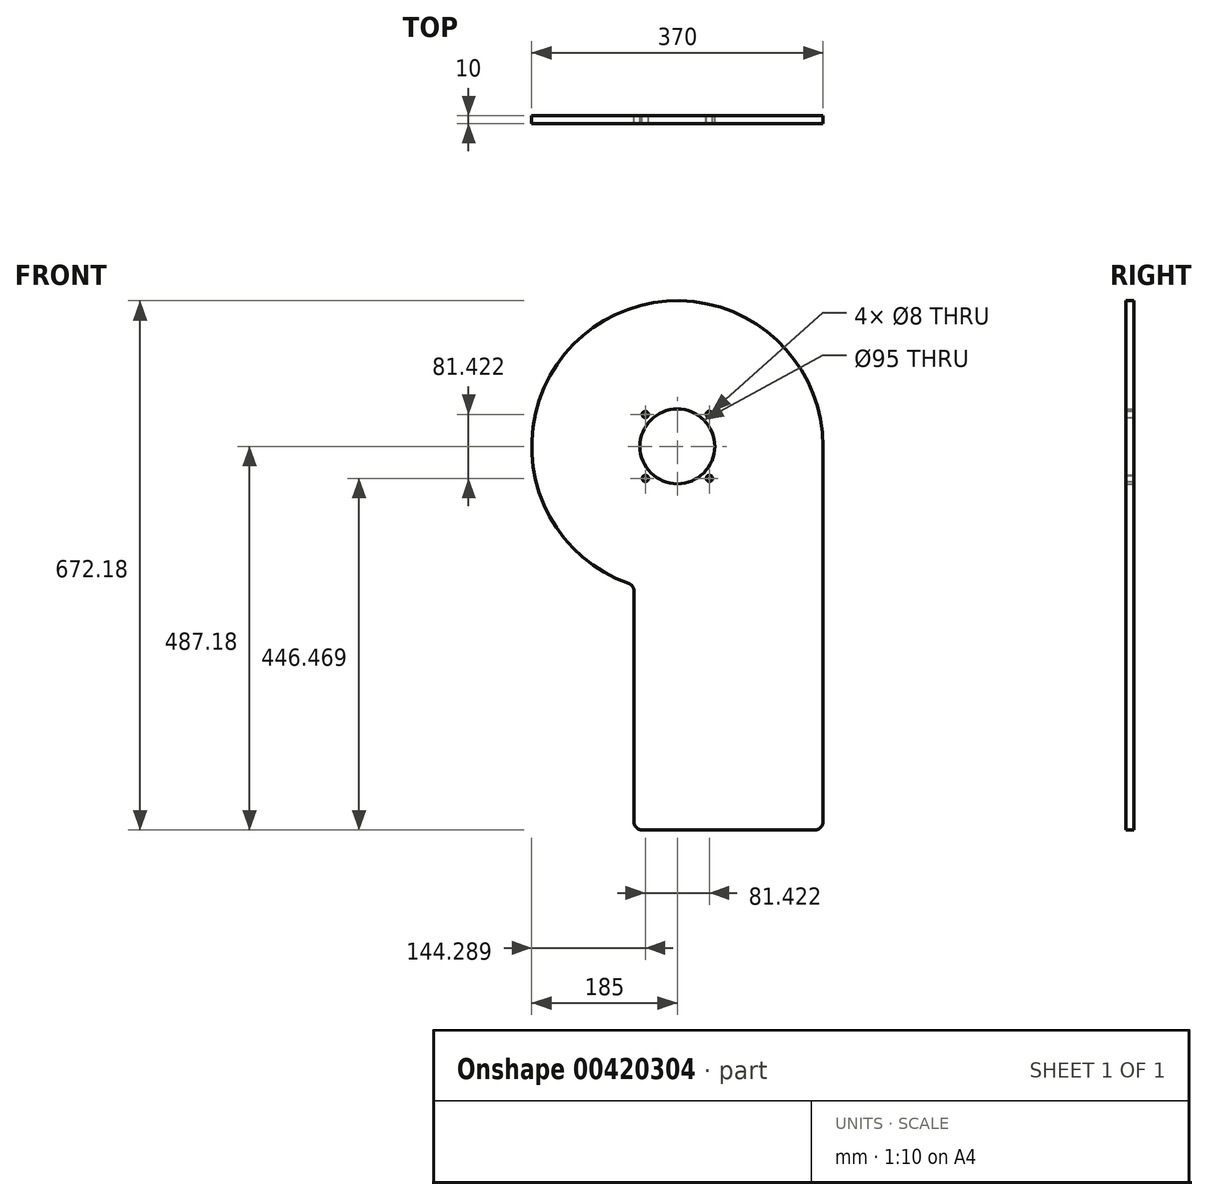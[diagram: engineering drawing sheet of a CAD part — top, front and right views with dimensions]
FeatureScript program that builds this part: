
annotation { "Feature Type Name" : "Feature", "Feature Type Description" : "" }
export const myFeature = defineFeature(function(context is Context, id is Id, definition is map)
    precondition{}
    {
        {
            var Q0;
            Q0=qCreatedBy(makeId("Front.planeOp"),FACE);
            var sketch = newSketch(context, id + "F0", { "sketchPlane" : qUnion([Q0])});
            skCircle(sketch, "E0", {"center": v(185, 1015) * mm, "radius": 47.5 * mm});
            skCircle(sketch, "E1", {"center": v(144.29, 1055.6) * mm, "radius": 4 * mm});
            skCircle(sketch, "E2", {"center": v(144.4, 974.29) * mm, "radius": 4 * mm});
            skCircle(sketch, "E3", {"center": v(225.71, 974.4) * mm, "radius": 4 * mm});
            skCircle(sketch, "E4", {"center": v(225.6, 1055.71) * mm, "radius": 4 * mm});
            skPoint(sketch, "E5.end.orphan", {"position": v(66.87, 0) * mm});
            skPoint(sketch, "E5.start.orphan", {"position": v(303.13, 0) * mm});
            skPoint(sketch, "E6.visualSharp", {"position": v(66.87, 528.91) * mm});
            skArc(sketch, "E6.filletArc", {"start": v(66.87, 538.91) * mm, "mid": v(69.8, 531.84) * mm, "end": v(76.87, 528.91) * mm});
            skPoint(sketch, "E7.visualSharp", {"position": v(303.13, 528.91) * mm});
            skArc(sketch, "E7.filletArc", {"start": v(293.13, 528.91) * mm, "mid": v(300.2, 531.84) * mm, "end": v(303.13, 538.91) * mm});
            skLineSegment(sketch, "E8", {"start": v(370, 1015) * mm, "end": v(370, 537.82) * mm});
            skLineSegment(sketch, "E9", {"start": v(360, 527.82) * mm, "end": v(140, 527.82) * mm});
            skLineSegment(sketch, "E10", {"start": v(130, 537.82) * mm, "end": v(130, 831.15) * mm});
            skArc(sketch, "E11", {"start": v(370, 1015) * mm, "mid": v(78.2, 1166.05) * mm, "end": v(123.33, 840.58) * mm});
            skPoint(sketch, "E12.visualSharp", {"position": v(130, 838.36) * mm});
            skArc(sketch, "E12.filletArc", {"start": v(130, 831.15) * mm, "mid": v(128.16, 836.93) * mm, "end": v(123.33, 840.58) * mm});
            skPoint(sketch, "E13.visualSharp", {"position": v(130, 527.82) * mm});
            skArc(sketch, "E13.filletArc", {"start": v(130, 537.82) * mm, "mid": v(132.93, 530.75) * mm, "end": v(140, 527.82) * mm});
            skPoint(sketch, "E14.visualSharp", {"position": v(370, 527.82) * mm});
            skArc(sketch, "E14.filletArc", {"start": v(360, 527.82) * mm, "mid": v(367.07, 530.75) * mm, "end": v(370, 537.82) * mm});
            skSolve(sketch);
        }
        {
            var Q0;
            Q0 = qSketchRegion(id + "F0", true);
            extrude(context, id + "F1", {"entities" : qUnion([Q0]), "depth" : 10 * mm});
        }
    });
